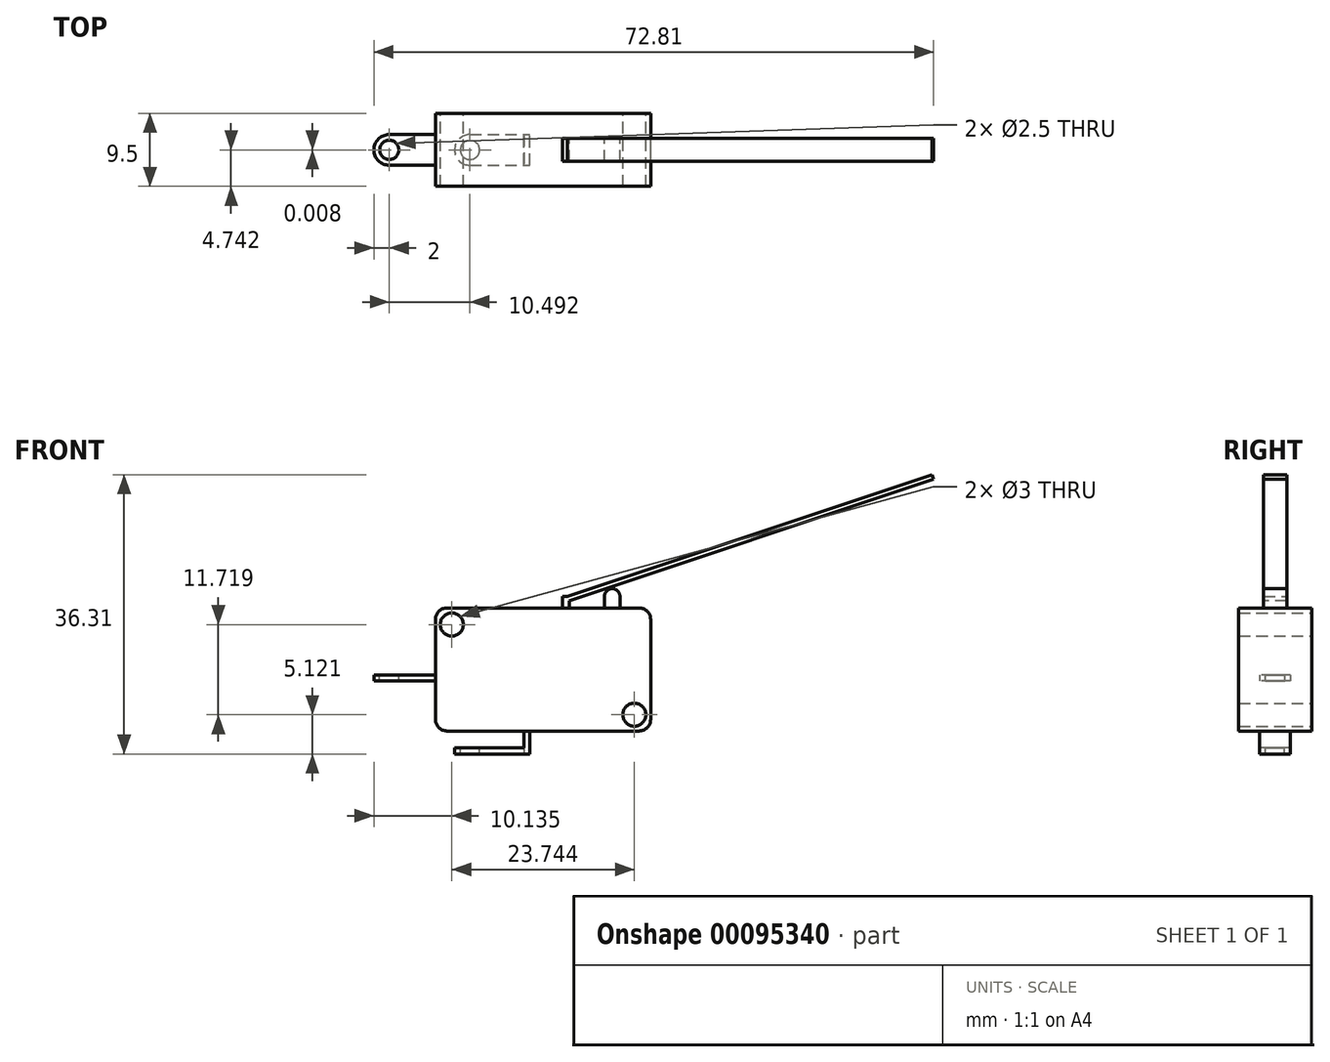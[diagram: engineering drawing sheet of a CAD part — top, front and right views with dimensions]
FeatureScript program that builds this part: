
annotation { "Feature Type Name" : "Feature", "Feature Type Description" : "" }
export const myFeature = defineFeature(function(context is Context, id is Id, definition is map)
    precondition{}
    {
        {
            var Q0;
            Q0=qCreatedBy(makeId("Front.planeOp"),FACE);
            var sketch = newSketch(context, id + "F0", { "sketchPlane" : qUnion([Q0])});
            skCircle(sketch, "E0", {"center": v(1.5, 14.5) * mm, "radius": 1.5 * mm});
            skCircle(sketch, "E1", {"center": v(25.88, 2.12) * mm, "radius": 1.5 * mm});
            skPoint(sketch, "E2", {"position": v(1.5, 16) * mm});
            skPoint(sketch, "E3", {"position": v(0, 14.5) * mm});
            skLineSegment(sketch, "E4", {"start": v(28, 0) * mm, "end": v(25.88, 2.12) * mm});
            skCircle(sketch, "E5", {"center": v(26.5, 1.5) * mm, "radius": 1.5 * mm});
            skLineSegment(sketch, "E6", {"start": v(0, 16) * mm, "end": v(2.11, 13.87) * mm});
            skCircle(sketch, "E7", {"center": v(2.13, 13.84) * mm, "radius": 1.5 * mm});
            skCircle(sketch, "E8", {"center": v(1.5, 1.5) * mm, "radius": 1.5 * mm});
            skCircle(sketch, "E9", {"center": v(26.5, 14.5) * mm, "radius": 1.5 * mm});
            skPoint(sketch, "E10", {"position": v(0, 1.5) * mm});
            skPoint(sketch, "E11", {"position": v(1.5, 0) * mm});
            skLineSegment(sketch, "E12", {"start": v(0, 14.5) * mm, "end": v(0, 1.5) * mm});
            skLineSegment(sketch, "E13", {"start": v(1.5, 0) * mm, "end": v(26.5, 0) * mm});
            skPoint(sketch, "E14", {"position": v(28, 1.5) * mm});
            skLineSegment(sketch, "E15", {"start": v(1.5, 16) * mm, "end": v(26.5, 16) * mm});
            skLineSegment(sketch, "E16", {"start": v(28, 1.5) * mm, "end": v(28, 14.5) * mm});
            skSolve(sketch);
        }
        {
            var Q0;
            {var subQ3=sQuery(id+"F0.wireOp",EDGE,"E12");Q0=makeQuery(id+"F0.imprint","IMPRINT",FACE,{"disambiguationData":[TD([[makeQuery(id+"F0.imprint","IMPRINT",EDGE,{"derivedFrom":subQ3}),1.0]])]});}
            var Q1;
            {var subQ0=sQuery(id+"F0.wireOp",EDGE,"E9");var subQ1=makeQuery(id+"F0.imprint","INTERSECT",VERTEX,{"derivedFrom":[subQ0,sQuery(id+"F0.wireOp",EDGE,"E15")]});Q1=makeQuery(id+"F0.imprint","IMPRINT",FACE,{"disambiguationData":[TD([[makeQuery(id+"F0.imprint","IMPRINT",EDGE,{"disambiguationData":[TD([[subQ1,1.0]])],"derivedFrom":subQ0}),1.0]])]});}
            var Q2;
            {var subQ0=sQuery(id+"F0.wireOp",EDGE,"E0");var subQ1=makeQuery(id+"F0.imprint","INTERSECT",VERTEX,{"derivedFrom":[subQ0,sQuery(id+"F0.wireOp",EDGE,"E15")]});Q2=makeQuery(id+"F0.imprint","IMPRINT",FACE,{"disambiguationData":[TD([[makeQuery(id+"F0.imprint","IMPRINT",EDGE,{"disambiguationData":[TD([[subQ1,1.0]])],"derivedFrom":subQ0}),1.0]])]});}
            var Q3;
            {var subQ0=sQuery(id+"F0.wireOp",EDGE,"E0");var subQ1=makeQuery(id+"F0.imprint","INTERSECT",VERTEX,{"derivedFrom":[subQ0,sQuery(id+"F0.wireOp",EDGE,"E12")]});Q3=makeQuery(id+"F0.imprint","IMPRINT",FACE,{"disambiguationData":[TD([[makeQuery(id+"F0.imprint","IMPRINT",EDGE,{"disambiguationData":[TD([[subQ1,1.0]])],"derivedFrom":subQ0}),1.0]])]});}
            var Q4;
            {var subQ0=sQuery(id+"F0.wireOp",EDGE,"E8");var subQ1=makeQuery(id+"F0.imprint","INTERSECT",VERTEX,{"derivedFrom":[subQ0,sQuery(id+"F0.wireOp",EDGE,"E12")]});Q4=makeQuery(id+"F0.imprint","IMPRINT",FACE,{"disambiguationData":[TD([[makeQuery(id+"F0.imprint","IMPRINT",EDGE,{"disambiguationData":[TD([[subQ1,-1.0]])],"derivedFrom":subQ0}),1.0]])]});}
            var Q5;
            {var subQ0=sQuery(id+"F0.wireOp",EDGE,"E4");var subQ1=sQuery(id+"F0.wireOp",EDGE,"E1");var subQ2=makeQuery(id+"F0.imprint","INTERSECT",VERTEX,{"derivedFrom":[subQ1,subQ0]});Q5=makeQuery(id+"F0.imprint","IMPRINT",FACE,{"disambiguationData":[TD([[makeQuery(id+"F0.imprint","IMPRINT",EDGE,{"disambiguationData":[TD([[subQ2,1.0]])],"derivedFrom":subQ1}),-1.0]])]});}
            var Q6;
            {var subQ0=sQuery(id+"F0.wireOp",EDGE,"E4");var subQ1=sQuery(id+"F0.wireOp",EDGE,"E1");var subQ2=makeQuery(id+"F0.imprint","INTERSECT",VERTEX,{"derivedFrom":[subQ1,subQ0]});Q6=makeQuery(id+"F0.imprint","IMPRINT",FACE,{"disambiguationData":[TD([[makeQuery(id+"F0.imprint","IMPRINT",EDGE,{"disambiguationData":[TD([[subQ2,-1.0]])],"derivedFrom":subQ1}),-1.0]])]});}
            extrude(context, id + "F1", {"entities" : qUnion([Q0, Q1, Q2, Q3, Q4, Q5, Q6]), "depth" : 9.5 * mm});
        }
        {
            var Q0;
            Q0=makeQuery(id+"F1.opExtrude","SWEPT_FACE",FACE,{"disambiguationData":[OSD([sQuery(id+"F0.wireOp",EDGE,"E12")])]});
            var sketch = newSketch(context, id + "F2", { "sketchPlane" : qUnion([Q0])});
            skLineSegment(sketch, "E17.bottom", {"start": v(2.75, 7.3) * mm, "end": v(6.75, 7.3) * mm});
            skLineSegment(sketch, "E17.top", {"start": v(2.75, 6.5) * mm, "end": v(6.75, 6.5) * mm});
            skLineSegment(sketch, "E17.left", {"start": v(2.75, 7.3) * mm, "end": v(2.75, 6.5) * mm});
            skLineSegment(sketch, "E17.right", {"start": v(6.75, 7.3) * mm, "end": v(6.75, 6.5) * mm});
            skSolve(sketch);
        }
        {
            var Q0;
            Q0=makeQuery(id+"F2.imprint","IMPRINT",FACE,{"disambiguationData":[TD([[makeQuery(id+"F2.imprint","IMPRINT",EDGE,{"derivedFrom":sQuery(id+"F2.wireOp",EDGE,"E17.bottom")}),-1.0]])]});
            extrude(context, id + "F3", {"entities" : qUnion([Q0]), "operationType" : NewBodyOperationType.ADD, "depth" : 8 * mm});
        }
        {
            var Q0;
            Q0=makeQuery(id+"F3.opExtrude","SWEPT_FACE",FACE,{"disambiguationData":[OSD([sQuery(id+"F2.wireOp",EDGE,"E17.bottom")])]});
            var sketch = newSketch(context, id + "F4", { "sketchPlane" : qUnion([Q0])});
            skCircle(sketch, "E18", {"center": v(-6, -4.75) * mm, "radius": 2 * mm});
            skCircle(sketch, "E19", {"center": v(-6, -4.75) * mm, "radius": 1.25 * mm});
            skSolve(sketch);
        }
        {
            var Q0;
            Q0=makeQuery(id+"F4.imprint","IMPRINT",FACE,{"disambiguationData":[TD([[makeQuery(id+"F4.imprint","IMPRINT",EDGE,{"derivedFrom":sQuery(id+"F4.wireOp",EDGE,"E19")}),1.0]])]});
            var Q1;
            {var subQ0=sQuery(id+"F4.wireOp",EDGE,"E18");var subQ1=sQuery(id+"F2.wireOp",EDGE,"E17.bottom");var subQ2=makeQuery(id+"F3.opExtrude","CAP_EDGE",EDGE,{"disambiguationData":[OSD([subQ1])],"isStart":false});var subQ3=makeQuery(id+"F4.imprint","INTERSECT",VERTEX,{"derivedFrom":[subQ2,subQ0]});Q1=makeQuery(id+"F4.imprint","IMPRINT",FACE,{"disambiguationData":[TD([[makeQuery(id+"F4.imprint","IMPRINT",EDGE,{"disambiguationData":[TD([[subQ3,1.0]])],"derivedFrom":subQ0}),-1.0]])]});}
            var Q2;
            {var subQ0=sQuery(id+"F4.wireOp",EDGE,"E18");var subQ1=sQuery(id+"F2.wireOp",EDGE,"E17.bottom");var subQ2=makeQuery(id+"F3.opExtrude","CAP_EDGE",EDGE,{"disambiguationData":[OSD([subQ1])],"isStart":false});var subQ3=makeQuery(id+"F4.imprint","INTERSECT",VERTEX,{"derivedFrom":[subQ2,subQ0]});Q2=makeQuery(id+"F4.imprint","IMPRINT",FACE,{"disambiguationData":[TD([[makeQuery(id+"F4.imprint","IMPRINT",EDGE,{"disambiguationData":[TD([[subQ3,-1.0]])],"derivedFrom":subQ0}),-1.0]])]});}
            extrude(context, id + "F5", {"entities" : qUnion([Q0, Q1, Q2]), "operationType" : NewBodyOperationType.REMOVE, "oppositeDirection" : true, "depth" : 25 * mm});
        }
        {
            var Q0;
            Q0=makeQuery(id+"F1.opExtrude","SWEPT_FACE",FACE,{"disambiguationData":[OSD([sQuery(id+"F0.wireOp",EDGE,"E13")])]});
            var sketch = newSketch(context, id + "F6", { "sketchPlane" : qUnion([Q0])});
            skLineSegment(sketch, "E20.bottom", {"start": v(11.5, 6.75) * mm, "end": v(12.3, 6.75) * mm});
            skLineSegment(sketch, "E20.top", {"start": v(11.5, 2.75) * mm, "end": v(12.3, 2.75) * mm});
            skLineSegment(sketch, "E20.left", {"start": v(11.5, 6.75) * mm, "end": v(11.5, 2.75) * mm});
            skLineSegment(sketch, "E20.right", {"start": v(12.3, 6.75) * mm, "end": v(12.3, 2.75) * mm});
            skSolve(sketch);
        }
        {
            var Q0;
            Q0=makeQuery(id+"F6.imprint","IMPRINT",FACE,{"disambiguationData":[TD([[makeQuery(id+"F6.imprint","IMPRINT",EDGE,{"derivedFrom":sQuery(id+"F6.wireOp",EDGE,"E20.bottom")}),-1.0]])]});
            extrude(context, id + "F7", {"entities" : qUnion([Q0]), "operationType" : NewBodyOperationType.ADD, "depth" : 3 * mm});
        }
        {
            var Q0;
            Q0=makeQuery(id+"F7.opExtrude","SWEPT_FACE",FACE,{"disambiguationData":[OSD([sQuery(id+"F6.wireOp",EDGE,"E20.left")])]});
            var sketch = newSketch(context, id + "F8", { "sketchPlane" : qUnion([Q0])});
            skLineSegment(sketch, "E21.bottom", {"start": v(2.77, -2.2) * mm, "end": v(6.75, -2.2) * mm});
            skLineSegment(sketch, "E21.top", {"start": v(2.77, -3) * mm, "end": v(6.75, -3) * mm});
            skLineSegment(sketch, "E21.left", {"start": v(2.77, -2.2) * mm, "end": v(2.77, -3) * mm});
            skLineSegment(sketch, "E21.right", {"start": v(6.75, -2.2) * mm, "end": v(6.75, -3) * mm});
            skSolve(sketch);
        }
        {
            var Q0;
            Q0=makeQuery(id+"F8.imprint","IMPRINT",FACE,{"disambiguationData":[TD([[makeQuery(id+"F8.imprint","IMPRINT",EDGE,{"derivedFrom":sQuery(id+"F8.wireOp",EDGE,"E21.bottom")}),-1.0]])]});
            extrude(context, id + "F9", {"entities" : qUnion([Q0]), "operationType" : NewBodyOperationType.ADD, "depth" : 9 * mm});
        }
        {
            var Q0;
            Q0=makeQuery(id+"F9.opExtrude","SWEPT_FACE",FACE,{"disambiguationData":[OSD([sQuery(id+"F8.wireOp",EDGE,"E21.bottom")])]});
            var sketch = newSketch(context, id + "F10", { "sketchPlane" : qUnion([Q0])});
            skCircle(sketch, "E22", {"center": v(4.5, -4.76) * mm, "radius": 2 * mm});
            skCircle(sketch, "E23", {"center": v(4.5, -4.76) * mm, "radius": 1.25 * mm});
            skSolve(sketch);
        }
        {
            var Q0;
            Q0=makeQuery(id+"F10.imprint","IMPRINT",FACE,{"disambiguationData":[TD([[makeQuery(id+"F10.imprint","IMPRINT",EDGE,{"derivedFrom":sQuery(id+"F10.wireOp",EDGE,"E23")}),1.0]])]});
            var Q1;
            {var subQ0=sQuery(id+"F10.wireOp",EDGE,"E22");var subQ1=sQuery(id+"F8.wireOp",EDGE,"E21.bottom");var subQ2=makeQuery(id+"F9.opExtrude","CAP_EDGE",EDGE,{"disambiguationData":[OSD([subQ1])],"isStart":false});var subQ3=makeQuery(id+"F10.imprint","INTERSECT",VERTEX,{"derivedFrom":[subQ2,subQ0]});Q1=makeQuery(id+"F10.imprint","IMPRINT",FACE,{"disambiguationData":[TD([[makeQuery(id+"F10.imprint","IMPRINT",EDGE,{"disambiguationData":[TD([[subQ3,1.0]])],"derivedFrom":subQ0}),-1.0]])]});}
            var Q2;
            {var subQ0=sQuery(id+"F10.wireOp",EDGE,"E22");var subQ1=sQuery(id+"F8.wireOp",EDGE,"E21.bottom");var subQ2=makeQuery(id+"F9.opExtrude","CAP_EDGE",EDGE,{"disambiguationData":[OSD([subQ1])],"isStart":false});var subQ3=makeQuery(id+"F10.imprint","INTERSECT",VERTEX,{"derivedFrom":[subQ2,subQ0]});Q2=makeQuery(id+"F10.imprint","IMPRINT",FACE,{"disambiguationData":[TD([[makeQuery(id+"F10.imprint","IMPRINT",EDGE,{"disambiguationData":[TD([[subQ3,-1.0]])],"derivedFrom":subQ0}),-1.0]])]});}
            extrude(context, id + "F11", {"entities" : qUnion([Q0, Q1, Q2]), "operationType" : NewBodyOperationType.REMOVE, "oppositeDirection" : true, "depth" : 25 * mm});
        }
        {
            var Q0;
            Q0=makeQuery(id+"F1.opExtrude","SWEPT_FACE",FACE,{"disambiguationData":[OSD([sQuery(id+"F0.wireOp",EDGE,"E15")])]});
            var sketch = newSketch(context, id + "F12", { "sketchPlane" : qUnion([Q0])});
            skLineSegment(sketch, "E24.bottom", {"start": v(24, -6.25) * mm, "end": v(22, -6.25) * mm});
            skLineSegment(sketch, "E24.top", {"start": v(24, -3.25) * mm, "end": v(22, -3.25) * mm});
            skLineSegment(sketch, "E24.left", {"start": v(24, -6.25) * mm, "end": v(24, -3.25) * mm});
            skLineSegment(sketch, "E24.right", {"start": v(22, -6.25) * mm, "end": v(22, -3.25) * mm});
            skLineSegment(sketch, "E25.bottom", {"start": v(17.4, -6.25) * mm, "end": v(16.5, -6.25) * mm});
            skLineSegment(sketch, "E25.top", {"start": v(17.4, -3.25) * mm, "end": v(16.5, -3.25) * mm});
            skLineSegment(sketch, "E25.left", {"start": v(17.4, -6.25) * mm, "end": v(17.4, -3.25) * mm});
            skLineSegment(sketch, "E25.right", {"start": v(16.5, -6.25) * mm, "end": v(16.5, -3.25) * mm});
            skPoint(sketch, "E26", {"position": v(16.5, -4.75) * mm});
            skPoint(sketch, "E27", {"position": v(22, -4.75) * mm});
            skPoint(sketch, "E28", {"position": v(24, -4.75) * mm});
            skSolve(sketch);
        }
        {
            var Q0;
            Q0=makeQuery(id+"F12.imprint","IMPRINT",FACE,{"disambiguationData":[TD([[makeQuery(id+"F12.imprint","IMPRINT",EDGE,{"derivedFrom":sQuery(id+"F12.wireOp",EDGE,"E24.bottom")}),-1.0]])]});
            extrude(context, id + "F13", {"entities" : qUnion([Q0]), "operationType" : NewBodyOperationType.ADD, "depth" : 2.5 * mm});
        }
        {
            var Q0;
            Q0=makeQuery(id+"F13.opExtrude","SWEPT_FACE",FACE,{"disambiguationData":[OSD([sQuery(id+"F12.wireOp",EDGE,"E24.top")])]});
            var sketch = newSketch(context, id + "F14", { "sketchPlane" : qUnion([Q0])});
            skCircle(sketch, "E29", {"center": v(-23, 17.5) * mm, "radius": 1 * mm});
            skSolve(sketch);
        }
        {
            var Q0;
            {var subQ0=sQuery(id+"F14.wireOp",EDGE,"E29");var subQ1=sQuery(id+"F12.wireOp",EDGE,"E24.top");var subQ2=makeQuery(id+"F13.opExtrude","CAP_EDGE",EDGE,{"disambiguationData":[OSD([subQ1])],"isStart":false});var subQ3=makeQuery(id+"F14.imprint","INTERSECT",VERTEX,{"derivedFrom":[subQ2,subQ0]});Q0=makeQuery(id+"F14.imprint","IMPRINT",FACE,{"disambiguationData":[TD([[makeQuery(id+"F14.imprint","IMPRINT",EDGE,{"disambiguationData":[TD([[subQ3,1.0]])],"derivedFrom":subQ0}),-1.0]])]});}
            var Q1;
            {var subQ0=sQuery(id+"F14.wireOp",EDGE,"E29");var subQ1=sQuery(id+"F12.wireOp",EDGE,"E24.top");var subQ2=makeQuery(id+"F13.opExtrude","CAP_EDGE",EDGE,{"disambiguationData":[OSD([subQ1])],"isStart":false});var subQ3=makeQuery(id+"F14.imprint","INTERSECT",VERTEX,{"derivedFrom":[subQ2,subQ0]});Q1=makeQuery(id+"F14.imprint","IMPRINT",FACE,{"disambiguationData":[TD([[makeQuery(id+"F14.imprint","IMPRINT",EDGE,{"disambiguationData":[TD([[subQ3,-1.0]])],"derivedFrom":subQ0}),-1.0]])]});}
            extrude(context, id + "F15", {"entities" : qUnion([Q0, Q1]), "operationType" : NewBodyOperationType.REMOVE, "oppositeDirection" : true, "depth" : 25 * mm});
        }
        {
            var Q0;
            Q0=makeQuery(id+"F12.imprint","IMPRINT",FACE,{"disambiguationData":[TD([[makeQuery(id+"F12.imprint","IMPRINT",EDGE,{"derivedFrom":sQuery(id+"F12.wireOp",EDGE,"E25.bottom")}),-1.0]])]});
            extrude(context, id + "F16", {"entities" : qUnion([Q0]), "operationType" : NewBodyOperationType.ADD, "depth" : 1.5 * mm});
        }
        {
            var Q0;
            Q0=makeQuery(id+"F16.opExtrude","SWEPT_FACE",FACE,{"disambiguationData":[OSD([sQuery(id+"F12.wireOp",EDGE,"E25.bottom")])]});
            var sketch = newSketch(context, id + "F17", { "sketchPlane" : qUnion([Q0])});
            skCircle(sketch, "E30", {"center": v(16.95, 17.05) * mm, "radius": 0.45 * mm});
            skLineSegment(sketch, "E31", {"start": v(17.18, 17.5) * mm, "end": v(17.4, 16.84) * mm});
            skSolve(sketch);
        }
        {
            var Q0;
            {var subQ0=sQuery(id+"F17.wireOp",EDGE,"E31");var subQ1=sQuery(id+"F17.wireOp",EDGE,"E30");var subQ2=makeQuery(id+"F17.imprint","INTERSECT",VERTEX,{"disambiguationData":[OD(0.0)],"derivedFrom":[subQ1,subQ0]});Q0=makeQuery(id+"F17.imprint","IMPRINT",FACE,{"disambiguationData":[TD([[makeQuery(id+"F17.imprint","IMPRINT",EDGE,{"disambiguationData":[TD([[subQ2,-1.0]])],"derivedFrom":subQ0}),1.0]])]});}
            var Q1;
            {var subQ0=sQuery(id+"F17.wireOp",EDGE,"E31");var subQ3=sQuery(id+"F12.wireOp",EDGE,"E25.bottom");var subQ6=makeQuery(id+"F16.opExtrude","CAP_EDGE",EDGE,{"disambiguationData":[OSD([subQ3])],"isStart":false});var subQ7=makeQuery(id+"F17.imprint","INTERSECT",VERTEX,{"derivedFrom":[subQ6,subQ0]});Q1=makeQuery(id+"F17.imprint","IMPRINT",FACE,{"disambiguationData":[TD([[makeQuery(id+"F17.imprint","IMPRINT",EDGE,{"disambiguationData":[TD([[subQ7,-1.0]])],"derivedFrom":subQ0}),1.0]])]});}
            extrude(context, id + "F18", {"entities" : qUnion([Q0, Q1]), "operationType" : NewBodyOperationType.REMOVE, "oppositeDirection" : true, "depth" : 25 * mm});
        }
        {
            var Q0;
            Q0=makeQuery(id+"F18.boolean.opBoolean","COPY",FACE,{"derivedFrom":makeQuery(id+"F18.opExtrude","SWEPT_FACE",FACE,{"disambiguationData":[OSD([sQuery(id+"F17.wireOp",EDGE,"E31")])]})});
            extrude(context, id + "F19", {"entities" : qUnion([Q0]), "operationType" : NewBodyOperationType.ADD, "depth" : 50 * mm});
        }
    });
